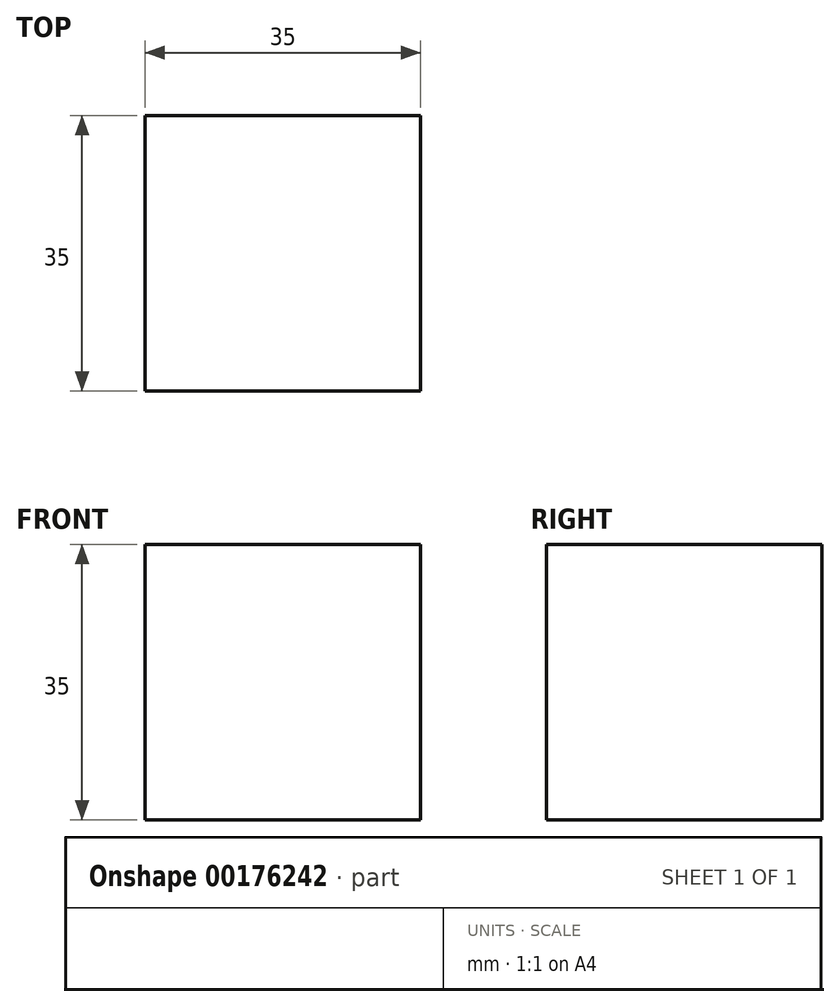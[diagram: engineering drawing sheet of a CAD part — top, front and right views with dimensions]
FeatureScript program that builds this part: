
annotation { "Feature Type Name" : "Feature", "Feature Type Description" : "" }
export const myFeature = defineFeature(function(context is Context, id is Id, definition is map)
    precondition{}
    {
        {
            var Q0;
            Q0=qCreatedBy(makeId("Top.planeOp"),FACE);
            var sketch = newSketch(context, id + "F0", { "sketchPlane" : qUnion([Q0])});
            skLineSegment(sketch, "E0.bottom", {"start": v(-17.5, 17.5) * mm, "end": v(17.5, 17.5) * mm});
            skLineSegment(sketch, "E0.top", {"start": v(-17.5, -17.5) * mm, "end": v(17.5, -17.5) * mm});
            skLineSegment(sketch, "E0.left", {"start": v(-17.5, 17.5) * mm, "end": v(-17.5, -17.5) * mm});
            skLineSegment(sketch, "E0.right", {"start": v(17.5, 17.5) * mm, "end": v(17.5, -17.5) * mm});
            skPoint(sketch, "E0.middle", {"position": v(0, 0) * mm});
            skSolve(sketch);
        }
        {
            var Q0;
            Q0=qSketchRegion(id+"F0",true);
            extrude(context, id + "F1", {"entities" : qUnion([Q0]), "depth" : 35 * mm});
        }
    });
